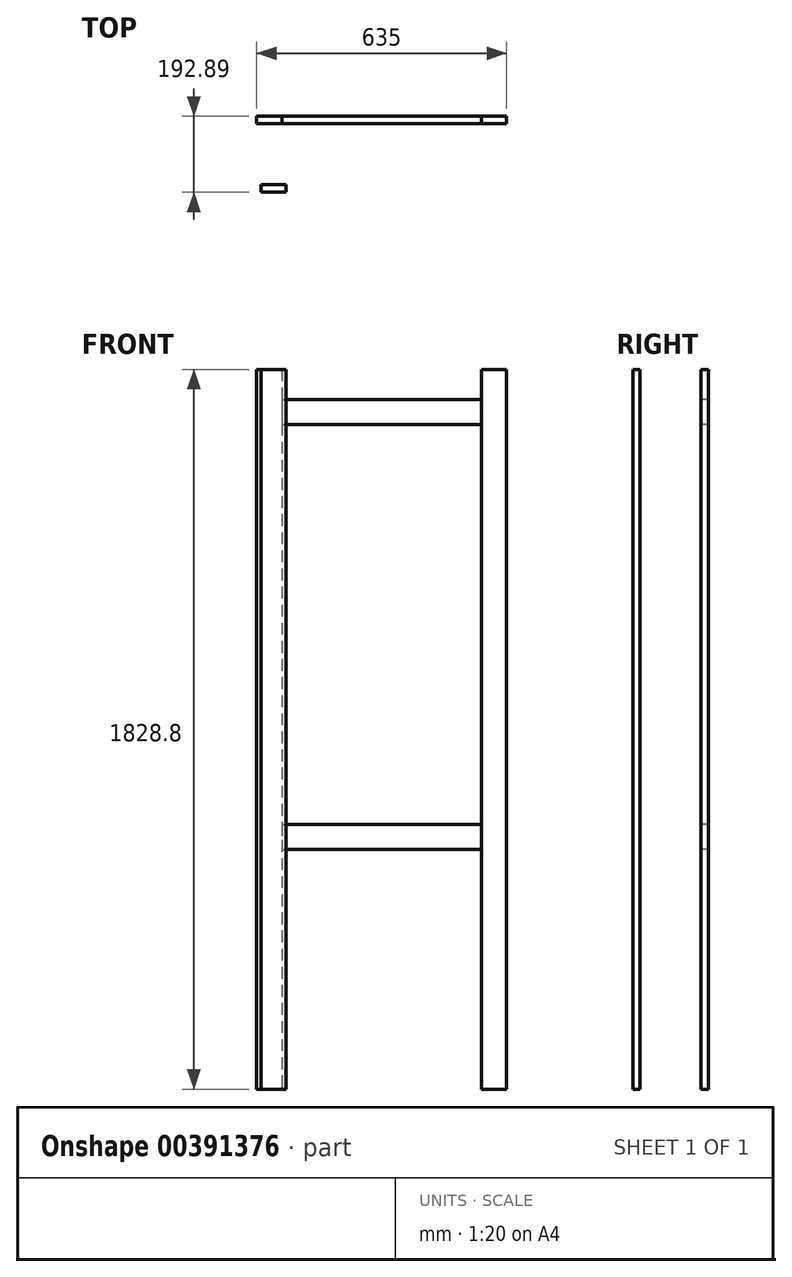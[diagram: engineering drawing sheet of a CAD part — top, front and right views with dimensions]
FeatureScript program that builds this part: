
annotation { "Feature Type Name" : "Feature", "Feature Type Description" : "" }
export const myFeature = defineFeature(function(context is Context, id is Id, definition is map)
    precondition{}
    {
        {
            var Q0;
            Q0=qCreatedBy(makeId("Top.planeOp"),FACE);
            var sketch = newSketch(context, id + "F0", { "sketchPlane" : qUnion([Q0])});
            skLineSegment(sketch, "E0.bottom", {"start": v(-73.73, 0) * mm, "end": v(-10.23, 0) * mm});
            skLineSegment(sketch, "E0.top", {"start": v(-73.73, 19.05) * mm, "end": v(-10.23, 19.05) * mm});
            skLineSegment(sketch, "E0.left", {"start": v(-73.73, 0) * mm, "end": v(-73.73, 19.05) * mm});
            skLineSegment(sketch, "E0.right", {"start": v(-10.23, 0) * mm, "end": v(-10.23, 19.05) * mm});
            skLineSegment(sketch, "E1.bottom", {"start": v(497.77, 19.05) * mm, "end": v(561.27, 19.05) * mm});
            skLineSegment(sketch, "E1.top", {"start": v(497.77, 0) * mm, "end": v(561.27, 0) * mm});
            skLineSegment(sketch, "E1.left", {"start": v(497.77, 19.05) * mm, "end": v(497.77, 0) * mm});
            skLineSegment(sketch, "E1.right", {"start": v(561.27, 19.05) * mm, "end": v(561.27, 0) * mm});
            skLineSegment(sketch, "E2.bottom", {"start": v(-63.5, -173.84) * mm, "end": v(0, -173.84) * mm});
            skLineSegment(sketch, "E2.top", {"start": v(-63.5, -154.79) * mm, "end": v(0, -154.79) * mm});
            skLineSegment(sketch, "E2.left", {"start": v(-63.5, -173.84) * mm, "end": v(-63.5, -154.79) * mm});
            skLineSegment(sketch, "E2.right", {"start": v(0, -173.84) * mm, "end": v(0, -154.79) * mm});
            skSolve(sketch);
        }
        {
            var Q0;
            Q0=makeQuery(id+"F0.imprint","IMPRINT",FACE,{"disambiguationData":[TD([[makeQuery(id+"F0.imprint","IMPRINT",EDGE,{"derivedFrom":sQuery(id+"F0.wireOp",EDGE,"E0.bottom")}),1.0]])]});
            extrude(context, id + "F1", {"entities" : qUnion([Q0]), "depth" : 1828.8 * mm});
        }
        {
            var Q0;
            Q0=makeQuery(id+"F0.imprint","IMPRINT",FACE,{"disambiguationData":[TD([[makeQuery(id+"F0.imprint","IMPRINT",EDGE,{"derivedFrom":sQuery(id+"F0.wireOp",EDGE,"E1.bottom")}),-1.0]])]});
            extrude(context, id + "F2", {"entities" : qUnion([Q0]), "depth" : 1828.8 * mm});
        }
        {
            var Q0;
            Q0=makeQuery(id+"F2.opExtrude","SWEPT_FACE",FACE,{"disambiguationData":[OSD([sQuery(id+"F0.wireOp",EDGE,"E1.left")])]});
            var sketch = newSketch(context, id + "F3", { "sketchPlane" : qUnion([Q0])});
            skLineSegment(sketch, "E3.bottom", {"start": v(-19.05, 1689.1) * mm, "end": v(0, 1689.1) * mm});
            skLineSegment(sketch, "E3.top", {"start": v(-19.05, 1752.6) * mm, "end": v(0, 1752.6) * mm});
            skLineSegment(sketch, "E3.left", {"start": v(-19.05, 1689.1) * mm, "end": v(-19.05, 1752.6) * mm});
            skLineSegment(sketch, "E3.right", {"start": v(0, 1689.1) * mm, "end": v(0, 1752.6) * mm});
            skLineSegment(sketch, "E4.bottom", {"start": v(-19.05, 609.6) * mm, "end": v(0, 609.6) * mm});
            skLineSegment(sketch, "E4.top", {"start": v(-19.05, 673.1) * mm, "end": v(0, 673.1) * mm});
            skLineSegment(sketch, "E4.left", {"start": v(-19.05, 609.6) * mm, "end": v(-19.05, 673.1) * mm});
            skLineSegment(sketch, "E4.right", {"start": v(0, 609.6) * mm, "end": v(0, 673.1) * mm});
            skSolve(sketch);
        }
        {
            var Q0;
            Q0=makeQuery(id+"F3.imprint","IMPRINT",FACE,{"disambiguationData":[TD([[makeQuery(id+"F3.imprint","IMPRINT",EDGE,{"derivedFrom":sQuery(id+"F3.wireOp",EDGE,"E3.bottom")}),1.0]])]});
            extrude(context, id + "F4", {"entities" : qUnion([Q0]), "endBound" : BoundingType.UP_TO_NEXT, "depth" : 25.4 * mm});
        }
        {
            var Q0;
            Q0=makeQuery(id+"F3.imprint","IMPRINT",FACE,{"disambiguationData":[TD([[makeQuery(id+"F3.imprint","IMPRINT",EDGE,{"derivedFrom":sQuery(id+"F3.wireOp",EDGE,"E4.bottom")}),1.0]])]});
            extrude(context, id + "F5", {"entities" : qUnion([Q0]), "endBound" : BoundingType.UP_TO_NEXT, "depth" : 25.4 * mm});
        }
        {
            var Q0;
            Q0=makeQuery(id+"F0.imprint","IMPRINT",FACE,{"disambiguationData":[TD([[makeQuery(id+"F0.imprint","IMPRINT",EDGE,{"derivedFrom":sQuery(id+"F0.wireOp",EDGE,"E2.bottom")}),1.0]])]});
            extrude(context, id + "F6", {"entities" : qUnion([Q0]), "depth" : 1828.8 * mm});
        }
    });
